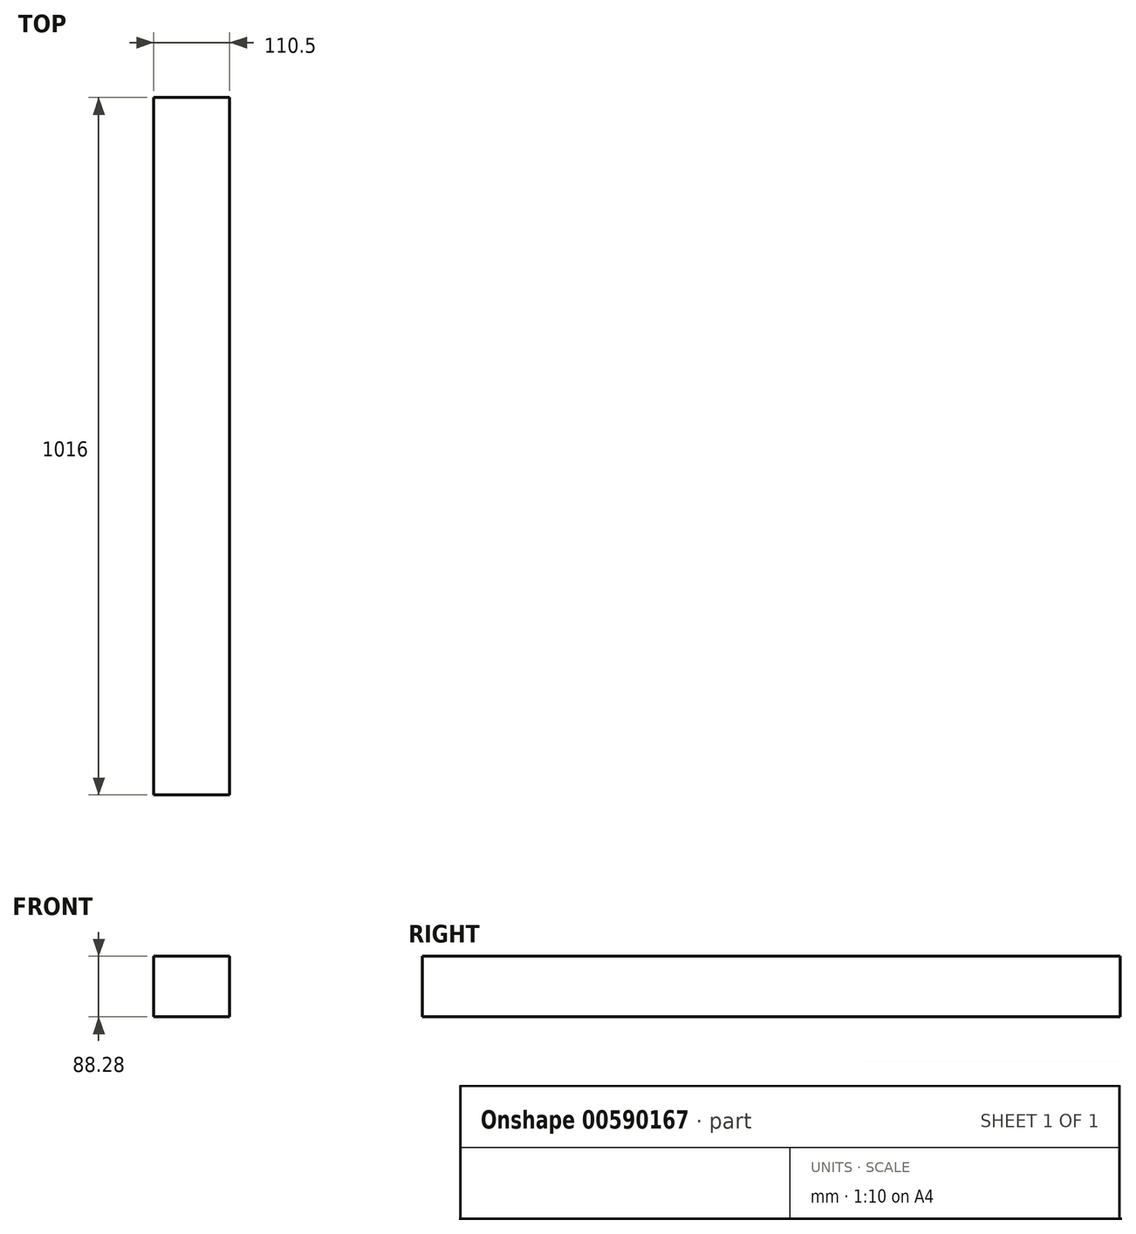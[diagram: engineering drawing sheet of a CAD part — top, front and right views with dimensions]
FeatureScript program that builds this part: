
annotation { "Feature Type Name" : "Feature", "Feature Type Description" : "" }
export const myFeature = defineFeature(function(context is Context, id is Id, definition is map)
    precondition{}
    {
        {
            var Q0;
            Q0=qCreatedBy(makeId("Front.planeOp"),FACE);
            var sketch = newSketch(context, id + "F0", { "sketchPlane" : qUnion([Q0])});
            skLineSegment(sketch, "E0.bottom", {"start": v(-55.25, -44.14) * mm, "end": v(55.25, -44.14) * mm});
            skLineSegment(sketch, "E0.top", {"start": v(-55.25, 44.14) * mm, "end": v(55.25, 44.14) * mm});
            skLineSegment(sketch, "E0.left", {"start": v(-55.25, -44.14) * mm, "end": v(-55.25, 44.14) * mm});
            skLineSegment(sketch, "E0.right", {"start": v(55.25, -44.14) * mm, "end": v(55.25, 44.14) * mm});
            skPoint(sketch, "E0.middle", {"position": v(0, 0) * mm});
            skSolve(sketch);
        }
        {
            var Q0;
            Q0=makeQuery(id+"F0.imprint","IMPRINT",FACE,{"disambiguationData":[TD([[makeQuery(id+"F0.imprint","IMPRINT",EDGE,{"derivedFrom":sQuery(id+"F0.wireOp",EDGE,"E0.bottom")}),1.0]])]});
            extrude(context, id + "F1", {"entities" : qUnion([Q0]), "endBound" : BoundingType.SYMMETRIC, "depth" : 1016 * mm, "offsetDistance" : 25.4 * mm});
        }
    });
